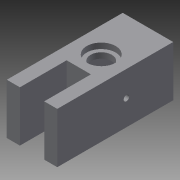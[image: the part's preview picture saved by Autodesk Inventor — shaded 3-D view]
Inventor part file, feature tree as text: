
AUTODESK INVENTOR PART (.ipt)
format: ipt  version: 2014 (Build 180170000, 170)  size: 171,008 bytes
history: native  units: mm
features: extrude x9, sketch x9, other x1
ambient origin geometry x8: Origin, YZ Plane, XZ Plane, XY Plane, X Axis, Y Axis, Z Axis, Center Point
bodies: Body1 (feature_tree)
feature tree (19):
  other  "Sólido1"
  extrude  "Extrusión1"  Depth=27.0mm
  extrude  "Extrusión2"  Depth=6.0mm
  extrude  "Extrusión3"  Depth=6.0mm
  extrude  "Extrusión4"  Depth=31.0mm TaperAngle=0.0deg
  extrude  "Extrusión5"  Depth=7.0mm
  extrude  "Extrusión6"  Depth=25.0mm TaperAngle=0.0deg
  extrude  "Extrusión8"  Depth=13.5mm
  extrude  "Extrusión9"  Depth=3.1mm
  extrude  "Extrusión10"  Depth=7.0mm TaperAngle=0.0deg
  sketch  "Boceto1"  dims[d0=27.0mm d1=27.0mm]
  sketch  "Boceto2"  dims[d2=62.0mm d3=0.0mm d4=6.0mm]
  sketch  "Boceto3"  dims[d5=6.0mm d6=6.0mm]
  sketch  "Boceto4"  dims[d7=6.0mm d8=31.0mm d9=0.0mm]
  sketch  "Boceto5"  dims[d10=7.0mm d11=7.0mm]
  sketch  "Boceto6"  dims[d12=25.0mm d13=30.0mm d14=0.0mm]
  sketch  "Boceto8"  dims[d16=5.1mm d17=13.5mm]
  sketch  "Boceto9"  dims[d18=23.0mm d19=3.1mm]
  sketch  "Boceto10"  dims[d20=13.5mm d22=7.0mm d23=0.0mm d24=15.5mm d25=13.5mm d27=3.0mm d28=0.0mm d29=11.3mm d31=3.0mm d32=0.0mm d33=6.0mm d34=6.0mm d42=13.5mm d43=3.0mm d44=3.0mm d45=0.0mm d47=12.0mm d48=3.0mm d49=3.5mm d50=3.5mm d51=3.5mm d52=3.5mm d53=3.0mm d54=3.0mm d55=3.5mm d56=3.5mm d57=3.5mm d58=3.5mm d59=3.0mm d60=6.0mm d61=0.0mm d62=3.0mm d63=7.5mm d64=7.5mm d65=6.0mm d66=0.0mm]
